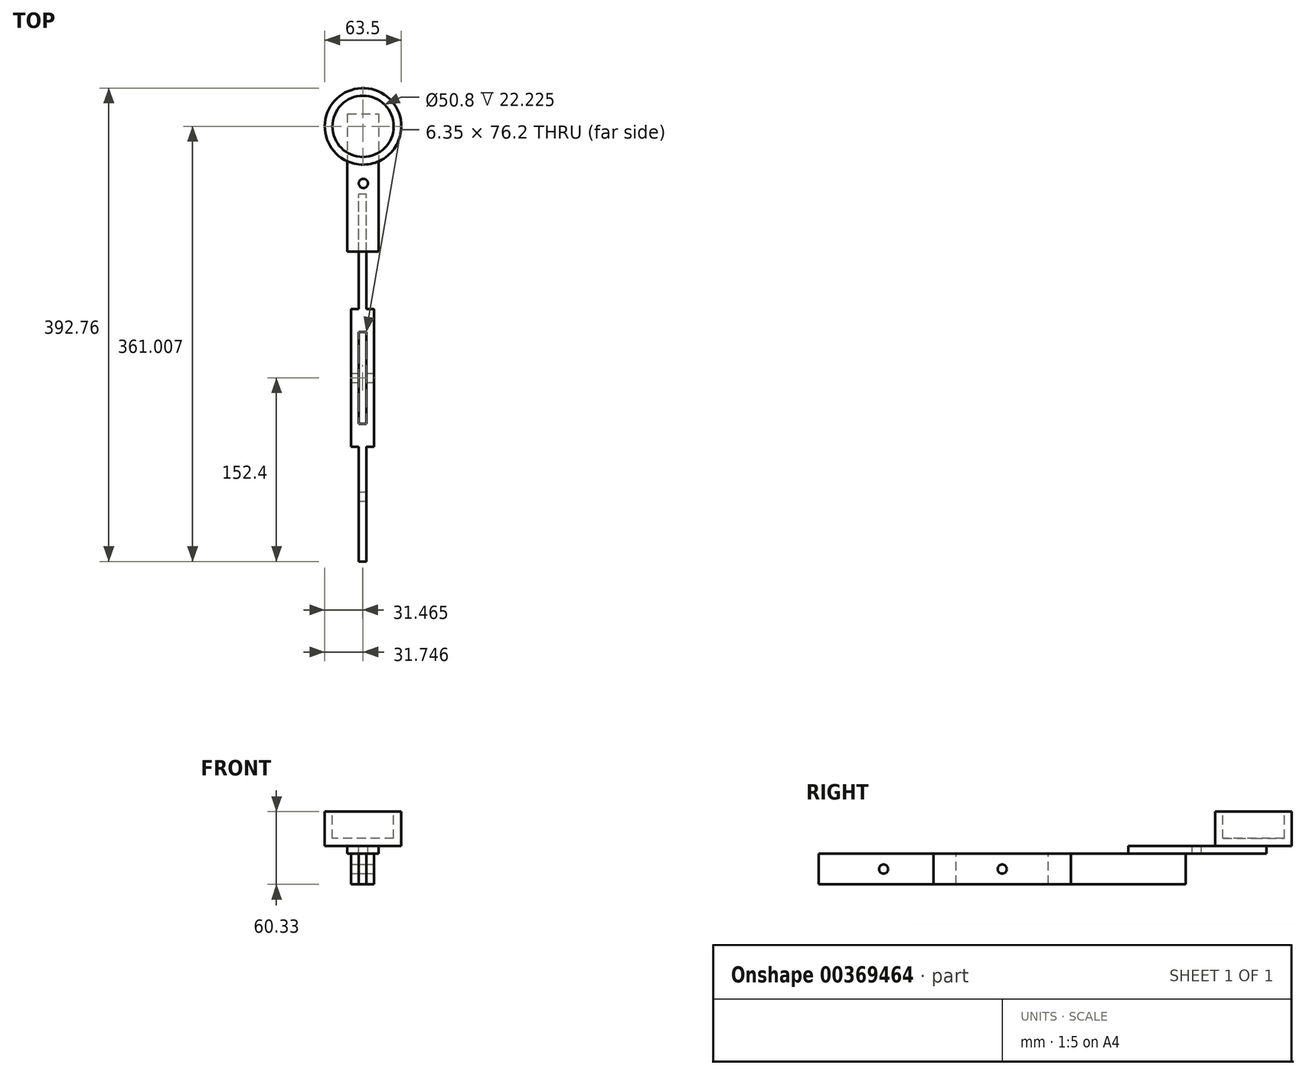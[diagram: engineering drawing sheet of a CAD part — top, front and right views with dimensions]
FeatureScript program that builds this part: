
annotation { "Feature Type Name" : "Feature", "Feature Type Description" : "" }
export const myFeature = defineFeature(function(context is Context, id is Id, definition is map)
    precondition{}
    {
        {
            var Q0;
            Q0=qCreatedBy(makeId("Right.planeOp"),FACE);
            var sketch = newSketch(context, id + "F0", { "sketchPlane" : qUnion([Q0])});
            skLineSegment(sketch, "E0.bottom", {"start": v(0, 0) * mm, "end": v(304.8, 0) * mm});
            skLineSegment(sketch, "E0.top", {"start": v(0, 25.4) * mm, "end": v(304.8, 25.4) * mm});
            skLineSegment(sketch, "E0.left", {"start": v(0, 0) * mm, "end": v(0, 25.4) * mm});
            skLineSegment(sketch, "E0.right", {"start": v(304.8, 0) * mm, "end": v(304.8, 25.4) * mm});
            skSolve(sketch);
        }
        {
            var Q0;
            Q0=qSketchRegion(id+"F0",true);
            extrude(context, id + "F1", {"entities" : qUnion([Q0]), "depth" : 19.05 * mm});
        }
        {
            var Q0;
            Q0=makeQuery(id+"F1.opExtrude","CAP_FACE",FACE,{"disambiguationData":[OSD([sQuery(id+"F0.wireOp",EDGE,"E0.bottom"),sQuery(id+"F0.wireOp",EDGE,"E0.top"),sQuery(id+"F0.wireOp",EDGE,"E0.left"),sQuery(id+"F0.wireOp",EDGE,"E0.right")])],"isStart":false});
            var sketch = newSketch(context, id + "F2", { "sketchPlane" : qUnion([Q0])});
            skLineSegment(sketch, "E1.bottom", {"start": v(0, 0) * mm, "end": v(95.25, 0) * mm});
            skLineSegment(sketch, "E1.top", {"start": v(0, 25.4) * mm, "end": v(95.25, 25.4) * mm});
            skLineSegment(sketch, "E1.left", {"start": v(0, 0) * mm, "end": v(0, 25.4) * mm});
            skLineSegment(sketch, "E1.right", {"start": v(95.25, 0) * mm, "end": v(95.25, 25.4) * mm});
            skSolve(sketch);
        }
        {
            var Q0;
            Q0=qSketchRegion(id+"F2",true);
            extrude(context, id + "F3", {"entities" : qUnion([Q0]), "operationType" : NewBodyOperationType.REMOVE, "oppositeDirection" : true, "depth" : 6.35 * mm});
        }
        {
            var Q0;
            Q0=makeQuery(id+"F1.opExtrude","CAP_FACE",FACE,{"disambiguationData":[OSD([sQuery(id+"F0.wireOp",EDGE,"E0.bottom"),sQuery(id+"F0.wireOp",EDGE,"E0.top"),sQuery(id+"F0.wireOp",EDGE,"E0.left"),sQuery(id+"F0.wireOp",EDGE,"E0.right")])],"isStart":true});
            var sketch = newSketch(context, id + "F4", { "sketchPlane" : qUnion([Q0])});
            skLineSegment(sketch, "E2.bottom", {"start": v(0, 25.4) * mm, "end": v(-95.25, 25.4) * mm});
            skLineSegment(sketch, "E2.top", {"start": v(0, 0) * mm, "end": v(-95.25, 0) * mm});
            skLineSegment(sketch, "E2.left", {"start": v(0, 25.4) * mm, "end": v(0, 0) * mm});
            skLineSegment(sketch, "E2.right", {"start": v(-95.25, 25.4) * mm, "end": v(-95.25, 0) * mm});
            skSolve(sketch);
        }
        {
            var Q0;
            Q0=makeQuery(id+"F4.imprint","IMPRINT",FACE,{"disambiguationData":[TD([[makeQuery(id+"F4.imprint","IMPRINT",EDGE,{"derivedFrom":sQuery(id+"F4.wireOp",EDGE,"E2.bottom")}),1.0]])]});
            extrude(context, id + "F5", {"entities" : qUnion([Q0]), "operationType" : NewBodyOperationType.REMOVE, "oppositeDirection" : true, "depth" : 6.35 * mm});
        }
        {
            var Q0;
            Q0=makeQuery(id+"F1.opExtrude","CAP_FACE",FACE,{"disambiguationData":[OSD([sQuery(id+"F0.wireOp",EDGE,"E0.bottom"),sQuery(id+"F0.wireOp",EDGE,"E0.top"),sQuery(id+"F0.wireOp",EDGE,"E0.left"),sQuery(id+"F0.wireOp",EDGE,"E0.right")])],"isStart":false});
            var sketch = newSketch(context, id + "F6", { "sketchPlane" : qUnion([Q0])});
            skLineSegment(sketch, "E3.bottom", {"start": v(304.8, 25.4) * mm, "end": v(209.55, 25.4) * mm});
            skLineSegment(sketch, "E3.top", {"start": v(304.8, 0) * mm, "end": v(209.55, 0) * mm});
            skLineSegment(sketch, "E3.left", {"start": v(304.8, 25.4) * mm, "end": v(304.8, 0) * mm});
            skLineSegment(sketch, "E3.right", {"start": v(209.55, 25.4) * mm, "end": v(209.55, 0) * mm});
            skSolve(sketch);
        }
        {
            var Q0;
            Q0=qSketchRegion(id+"F6",true);
            extrude(context, id + "F7", {"entities" : qUnion([Q0]), "operationType" : NewBodyOperationType.REMOVE, "oppositeDirection" : true, "depth" : 6.35 * mm});
        }
        {
            var Q0;
            Q0=makeQuery(id+"F1.opExtrude","CAP_FACE",FACE,{"disambiguationData":[OSD([sQuery(id+"F0.wireOp",EDGE,"E0.bottom"),sQuery(id+"F0.wireOp",EDGE,"E0.top"),sQuery(id+"F0.wireOp",EDGE,"E0.left"),sQuery(id+"F0.wireOp",EDGE,"E0.right")])],"isStart":true});
            var sketch = newSketch(context, id + "F8", { "sketchPlane" : qUnion([Q0])});
            skLineSegment(sketch, "E4.bottom", {"start": v(-304.8, 0) * mm, "end": v(-209.55, 0) * mm});
            skLineSegment(sketch, "E4.top", {"start": v(-304.8, 25.4) * mm, "end": v(-209.55, 25.4) * mm});
            skLineSegment(sketch, "E4.left", {"start": v(-304.8, 0) * mm, "end": v(-304.8, 25.4) * mm});
            skLineSegment(sketch, "E4.right", {"start": v(-209.55, 0) * mm, "end": v(-209.55, 25.4) * mm});
            skSolve(sketch);
        }
        {
            var Q0;
            Q0=qSketchRegion(id+"F8",true);
            extrude(context, id + "F9", {"entities" : qUnion([Q0]), "operationType" : NewBodyOperationType.REMOVE, "oppositeDirection" : true, "depth" : 6.35 * mm});
        }
        {
            var Q0;
            Q0=makeQuery(id+"F1.opExtrude","SWEPT_FACE",FACE,{"disambiguationData":[OSD([sQuery(id+"F0.wireOp",EDGE,"E0.top")])]});
            var sketch = newSketch(context, id + "F10", { "sketchPlane" : qUnion([Q0])});
            skLineSegment(sketch, "E5.bottom", {"start": v(6.35, 190.5) * mm, "end": v(12.7, 190.5) * mm});
            skLineSegment(sketch, "E5.top", {"start": v(6.35, 114.3) * mm, "end": v(12.7, 114.3) * mm});
            skLineSegment(sketch, "E5.left", {"start": v(6.35, 190.5) * mm, "end": v(6.35, 114.3) * mm});
            skLineSegment(sketch, "E5.right", {"start": v(12.7, 190.5) * mm, "end": v(12.7, 114.3) * mm});
            skSolve(sketch);
        }
        {
            var Q0;
            Q0=qSketchRegion(id+"F10",true);
            extrude(context, id + "F11", {"entities" : qUnion([Q0]), "operationType" : NewBodyOperationType.REMOVE, "oppositeDirection" : true, "depth" : 25.4 * mm});
        }
        {
            var Q0;
            Q0=makeQuery(id+"F1.opExtrude","CAP_FACE",FACE,{"disambiguationData":[OSD([sQuery(id+"F0.wireOp",EDGE,"E0.bottom"),sQuery(id+"F0.wireOp",EDGE,"E0.top"),sQuery(id+"F0.wireOp",EDGE,"E0.left"),sQuery(id+"F0.wireOp",EDGE,"E0.right")])],"isStart":false});
            var sketch = newSketch(context, id + "F12", { "sketchPlane" : qUnion([Q0])});
            skCircle(sketch, "E6", {"center": v(152.4, 12.7) * mm, "radius": 3.81 * mm});
            skPoint(sketch, "E6.centerSnap0", {"position": v(152.4, 25.4) * mm});
            skSolve(sketch);
        }
        {
            var Q0;
            Q0=qSketchRegion(id+"F12",true);
            extrude(context, id + "F13", {"entities" : qUnion([Q0]), "operationType" : NewBodyOperationType.REMOVE, "oppositeDirection" : true, "depth" : 25.4 * mm});
        }
        {
            var Q0;
            Q0=makeQuery(id+"F1.opExtrude","SWEPT_FACE",FACE,{"disambiguationData":[OSD([sQuery(id+"F0.wireOp",EDGE,"E0.top")])]});
            var sketch = newSketch(context, id + "F14", { "sketchPlane" : qUnion([Q0])});
            skLineSegment(sketch, "E7.bottom", {"start": v(-3.18, 371.48) * mm, "end": v(22.79, 371.48) * mm});
            skLineSegment(sketch, "E7.top", {"start": v(-3.17, 257.18) * mm, "end": v(22.79, 257.18) * mm});
            skLineSegment(sketch, "E7.left", {"start": v(-3.18, 371.48) * mm, "end": v(-3.17, 257.18) * mm});
            skLineSegment(sketch, "E7.right", {"start": v(22.79, 371.48) * mm, "end": v(22.79, 257.18) * mm});
            skSolve(sketch);
        }
        {
            var Q0;
            Q0=qSketchRegion(id+"F14",true);
            extrude(context, id + "F15", {"entities" : qUnion([Q0]), "operationType" : NewBodyOperationType.ADD, "depth" : 6.35 * mm});
        }
        {
            var Q0;
            Q0=makeQuery(id+"F15.opExtrude","CAP_FACE",FACE,{"disambiguationData":[OSD([sQuery(id+"F14.wireOp",EDGE,"E7.bottom"),sQuery(id+"F14.wireOp",EDGE,"E7.top"),sQuery(id+"F14.wireOp",EDGE,"E7.left"),sQuery(id+"F14.wireOp",EDGE,"E7.right")])],"isStart":false});
            var sketch = newSketch(context, id + "F16", { "sketchPlane" : qUnion([Q0])});
            skCircle(sketch, "E8", {"center": v(10.09, 313.7) * mm, "radius": 3.81 * mm});
            skSolve(sketch);
        }
        {
            var Q0;
            Q0=qSketchRegion(id+"F16",true);
            extrude(context, id + "F17", {"entities" : qUnion([Q0]), "operationType" : NewBodyOperationType.REMOVE, "oppositeDirection" : true, "depth" : 25.4 * mm});
        }
        {
            var Q0;
            Q0=makeQuery(id+"F3.boolean.opBoolean","COPY",FACE,{"derivedFrom":makeQuery(id+"F3.opExtrude","CAP_FACE",FACE,{"disambiguationData":[OSD([sQuery(id+"F2.wireOp",EDGE,"E1.bottom"),sQuery(id+"F2.wireOp",EDGE,"E1.top"),sQuery(id+"F2.wireOp",EDGE,"E1.left"),sQuery(id+"F2.wireOp",EDGE,"E1.right")])],"isStart":false})});
            var sketch = newSketch(context, id + "F18", { "sketchPlane" : qUnion([Q0])});
            skCircle(sketch, "E9", {"center": v(53.98, 12.7) * mm, "radius": 3.8 * mm});
            skSolve(sketch);
        }
        {
            var Q0;
            Q0=qSketchRegion(id+"F18",true);
            extrude(context, id + "F19", {"entities" : qUnion([Q0]), "operationType" : NewBodyOperationType.REMOVE, "oppositeDirection" : true, "depth" : 25.4 * mm});
        }
        {
            var Q0;
            Q0=makeQuery(id+"F15.opExtrude","CAP_FACE",FACE,{"disambiguationData":[OSD([sQuery(id+"F14.wireOp",EDGE,"E7.bottom"),sQuery(id+"F14.wireOp",EDGE,"E7.top"),sQuery(id+"F14.wireOp",EDGE,"E7.left"),sQuery(id+"F14.wireOp",EDGE,"E7.right")])],"isStart":false});
            var sketch = newSketch(context, id + "F20", { "sketchPlane" : qUnion([Q0])});
            skCircle(sketch, "E10", {"center": v(9.8, 361) * mm, "radius": 31.75 * mm});
            skPoint(sketch, "E10.centerSnap0", {"position": v(9.8, 257.18) * mm});
            skSolve(sketch);
        }
        {
            var Q0;
            Q0=qSketchRegion(id+"F20",true);
            extrude(context, id + "F21", {"entities" : qUnion([Q0]), "operationType" : NewBodyOperationType.ADD, "depth" : 28.57 * mm});
        }
        {
            var Q0;
            Q0=makeQuery(id+"F21.opExtrude","CAP_FACE",FACE,{"disambiguationData":[OSD([sQuery(id+"F20.wireOp",EDGE,"E10")])],"isStart":false});
            var sketch = newSketch(context, id + "F22", { "sketchPlane" : qUnion([Q0])});
            skCircle(sketch, "E11", {"center": v(9.8, 361) * mm, "radius": 25.4 * mm});
            skSolve(sketch);
        }
        {
            var Q0;
            Q0=qSketchRegion(id+"F22",true);
            extrude(context, id + "F23", {"entities" : qUnion([Q0]), "operationType" : NewBodyOperationType.REMOVE, "oppositeDirection" : true, "depth" : 22.22 * mm});
        }
    });
